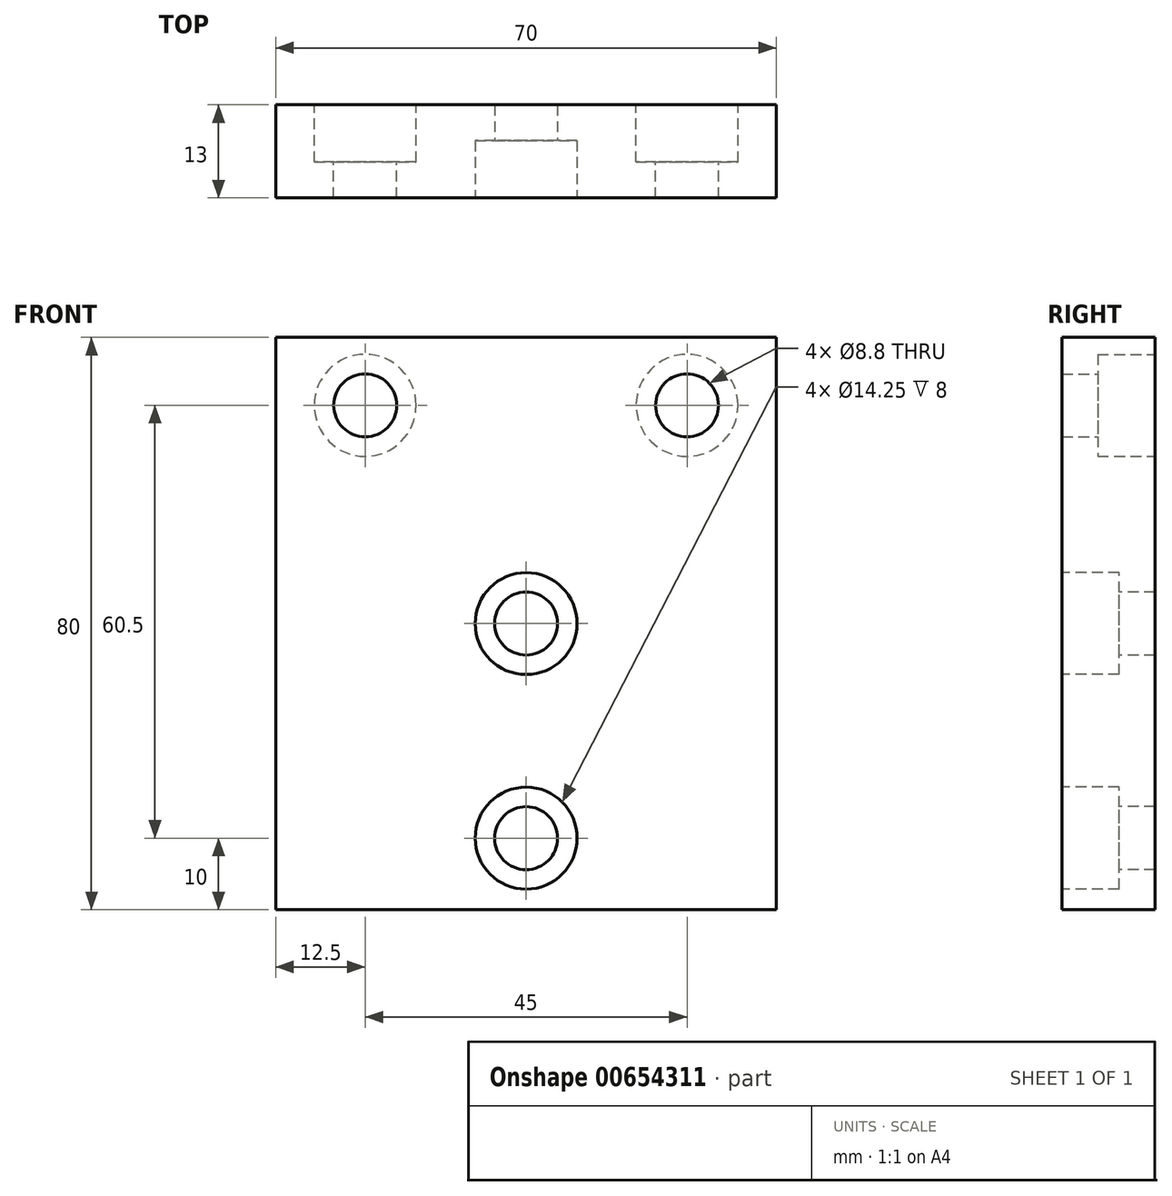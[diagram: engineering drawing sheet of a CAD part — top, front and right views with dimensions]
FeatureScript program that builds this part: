
annotation { "Feature Type Name" : "Feature", "Feature Type Description" : "" }
export const myFeature = defineFeature(function(context is Context, id is Id, definition is map)
    precondition{}
    {
        {
            var Q0;
            Q0=qCreatedBy(makeId("Front.planeOp"),FACE);
            var sketch = newSketch(context, id + "F0", { "sketchPlane" : qUnion([Q0])});
            skLineSegment(sketch, "E0.bottom", {"start": v(35, 40) * mm, "end": v(-35, 40) * mm});
            skLineSegment(sketch, "E0.top", {"start": v(35, -40) * mm, "end": v(-35, -40) * mm});
            skLineSegment(sketch, "E0.left", {"start": v(35, 40) * mm, "end": v(35, -40) * mm});
            skLineSegment(sketch, "E0.right", {"start": v(-35, 40) * mm, "end": v(-35, -40) * mm});
            skPoint(sketch, "E0.middle", {"position": v(0, 0) * mm});
            skSolve(sketch);
        }
        {
            var Q0;
            Q0=makeQuery(id+"F0.imprint","IMPRINT",FACE,{"disambiguationData":[TD([[makeQuery(id+"F0.imprint","IMPRINT",EDGE,{"derivedFrom":sQuery(id+"F0.wireOp",EDGE,"E0.bottom")}),1.0]])]});
            extrude(context, id + "F1", {"entities" : qUnion([Q0]), "depth" : 13 * mm, "offsetDistance" : 25 * mm});
        }
        {
            var Q0;
            Q0=makeQuery(id+"F1.opExtrude","CAP_FACE",FACE,{"disambiguationData":[OSD([sQuery(id+"F0.wireOp",EDGE,"E0.bottom"),sQuery(id+"F0.wireOp",EDGE,"E0.top"),sQuery(id+"F0.wireOp",EDGE,"E0.left"),sQuery(id+"F0.wireOp",EDGE,"E0.right")])],"isStart":false});
            var sketch = newSketch(context, id + "F2", { "sketchPlane" : qUnion([Q0])});
            skPoint(sketch, "E1", {"position": v(0, -30) * mm});
            skPoint(sketch, "E2", {"position": v(0, 0) * mm});
            skSolve(sketch);
        }
        {
            var Q0;
            Q0=makeQuery(id+"F1.opExtrude","CAP_FACE",FACE,{"disambiguationData":[OSD([sQuery(id+"F0.wireOp",EDGE,"E0.bottom"),sQuery(id+"F0.wireOp",EDGE,"E0.top"),sQuery(id+"F0.wireOp",EDGE,"E0.left"),sQuery(id+"F0.wireOp",EDGE,"E0.right")])],"isStart":true});
            var sketch = newSketch(context, id + "F3", { "sketchPlane" : qUnion([Q0])});
            skPoint(sketch, "E3", {"position": v(-22.5, 30.5) * mm});
            skPoint(sketch, "E4", {"position": v(22.5, 30.5) * mm});
            skSolve(sketch);
        }
        {
            var Q0;
            Q0=sQuery(id+"F3.wireOp",VERTEX,"E3");
            var Q1;
            Q1=sQuery(id+"F3.wireOp",VERTEX,"E4");
            var Q2;
            Q2=makeQuery(id+"F1.opExtrude","SWEPT_BODY",BODY,{"disambiguationData":[OSD([sQuery(id+"F0.wireOp",EDGE,"E0.bottom"),sQuery(id+"F0.wireOp",EDGE,"E0.top"),sQuery(id+"F0.wireOp",EDGE,"E0.left"),sQuery(id+"F0.wireOp",EDGE,"E0.right")])]});
            hole(context, id + "F4", {"style" : HoleStyle.C_BORE, "endStyle" : HoleEndStyle.BLIND, "standardTappedOrClearance" : lookupTablePath({ "standard" : "ISO", "fit" : "Normal", "size" : "M8", "type" : "Clearance" }), "standardBlindInLast" : lookupTablePath({ "fit" : "Standard", "standard" : "ISO", "size" : "M8", "type" : "Clearance" }), "holeDiameter" : 8.8 * mm, "cBoreDiameter" : 14.25 * mm, "cBoreDepth" : 8 * mm, "majorDiameter" : 5 * mm, "holeDepth" : 22.75 * mm, "isTappedThrough" : true, "tappedDepth" : 19 * mm, "tapClearance" : 3, "startFromSketch" : true, "locations" : qUnion([Q0, Q1]), "scope" : qUnion([Q2])});
        }
        {
            var Q0;
            Q0=sQuery(id+"F2.wireOp",VERTEX,"E2");
            var Q1;
            Q1=sQuery(id+"F2.wireOp",VERTEX,"E1");
            var Q2;
            Q2=makeQuery(id+"F1.opExtrude","SWEPT_BODY",BODY,{"disambiguationData":[OSD([sQuery(id+"F0.wireOp",EDGE,"E0.bottom"),sQuery(id+"F0.wireOp",EDGE,"E0.top"),sQuery(id+"F0.wireOp",EDGE,"E0.left"),sQuery(id+"F0.wireOp",EDGE,"E0.right")])]});
            hole(context, id + "F5", {"style" : HoleStyle.C_BORE, "endStyle" : HoleEndStyle.BLIND, "standardTappedOrClearance" : lookupTablePath({ "standard" : "ISO", "fit" : "Normal", "size" : "M8", "type" : "Clearance" }), "standardBlindInLast" : lookupTablePath({ "fit" : "Standard", "standard" : "ISO", "size" : "M8", "type" : "Clearance" }), "holeDiameter" : 8.8 * mm, "cBoreDiameter" : 14.25 * mm, "cBoreDepth" : 8 * mm, "majorDiameter" : 5 * mm, "holeDepth" : 22.75 * mm, "isTappedThrough" : true, "tappedDepth" : 19 * mm, "tapClearance" : 3, "startFromSketch" : true, "locations" : qUnion([Q0, Q1]), "scope" : qUnion([Q2])});
        }
    });
